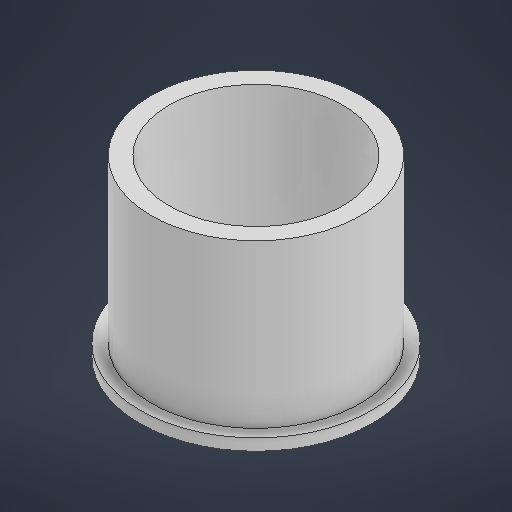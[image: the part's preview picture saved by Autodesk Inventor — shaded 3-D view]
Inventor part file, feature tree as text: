
AUTODESK INVENTOR PART (.ipt)
format: ipt  version: 2025 (Build 290162000, 162)  size: 303,104 bytes
history: native  units: in
note: dims shown in document units (in); Inventor stores cm internally (conversion verified against a paired STEP export)
features: other x12, extrude x8, sketch x6, fillet x5, plane x1
ambient origin geometry x8: Origin, YZ Plane, XZ Plane, XY Plane, X Axis, Y Axis, Z Axis, Center Point
bodies: Solid1 (feature_tree)
feature tree (32):
  other  "Table"
  other  "Cylinder Segment - 01"
  other  "Cylinder Segment - 02"
  other  "Cylinder Segment - 03"
  other  "Cylinder Segment - 04"
  other  "Cylinder Segment - 05"
  other  "Cylinder Segment - 06"
  other  "Cylinder Segment - 07"
  other  "Cylinder Segment - 08"
  other  "Cylinder Segment - 09"
  other  "Cylinder Segment - 10"
  other  "Cylinder Segment - Face"
  sketch  "Sketch1"  dims[d5=0.0in d7=0.0in]
  extrude  "Extrusion1"  TaperAngle=0.0deg  [1 undecoded]
  extrude  "Extrusion2"  Depth=10.0394in
  extrude  "Extrusion7"  Depth=0.3937in
  plane  "Work Plane2"
  extrude  "Extrusion8"  Depth=3.937in TaperAngle=360.0deg
  sketch  "Sketch24"  dims[d234=0.0787in d235=2.5591in]
  extrude  "Extrusion30"  Depth=2.5591in
  extrude  "Extrusion31"  Depth=0.3937in
  extrude  "Extrusion32"  Depth=0.3937in
  fillet  "Fillet14"  Radius=10.6299in
  fillet  "Fillet15"  Radius=3.5433in
  fillet  "Fillet16"  Radius=6.033in
  fillet  "Fillet17"  Radius=8.9897in
  fillet  "Fillet18"  Radius=0.0787in
  extrude  "Extrusion33"  Depth=0.3937in
  sketch  "Sketch2"  dims[d18=0.0in d27=10.0394in]
  sketch  "Sketch3"  dims[d33=0.3937in d34=0.0in d52=4.5276in]
  sketch  "Sketch Circular Pattern4"  dims[d229=0.2165in d230=3.937in d232=360.0deg]
  sketch  "Sketch25"  dims[d237=0.0591in d238=0.4375in d240=0.8253in d241=10.6299in d242=3.5433in d243=6.033in d244=8.9897in d247=0.0787in d248=5.1083in d249=3.6614in d250=0.0in d251=3.6614in d252=0.0in d253=9.4488in d254=0.3937in d255=0.0in d256=0.3937in d257=0.3937in d258=0.0787in d259=0.1969in d260=0.1969in d261=0.3937in d262=0.0in d113=0.0197in d114=0.0344in d115=0.0197in d116=0.0344in d167=0.0197in d168=0.0344in d169=0.0197in d170=0.0344in d215=0.0197in d216=0.0344in d217=0.0197in d218=0.0344in d219=0.0in d220=0.0in]
note: 1 required parameter value undecoded (feature->parameter linkage not recoverable at this tier; creation-order binding heuristic only, values carry confidence <= 0.55)
